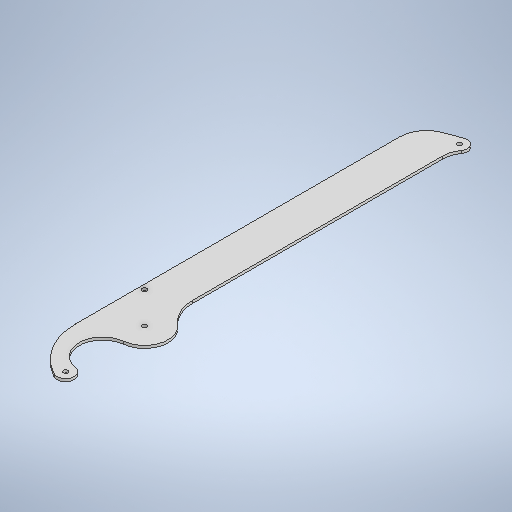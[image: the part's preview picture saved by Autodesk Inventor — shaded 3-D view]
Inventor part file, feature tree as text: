
AUTODESK INVENTOR PART (.ipt)
format: ipt  version: 2025.2 (Build 292293000, 293)  size: 292,864 bytes
history: native  units: in
note: dims shown in document units (in); Inventor stores cm internally (conversion verified against a paired STEP export)
features: extrude x2, sketch x2
ambient origin geometry x8: Origin, YZ Plane, XZ Plane, XY Plane, X Axis, Y Axis, Z Axis, Center Point
bodies: Solid1 (feature_tree)
feature tree (4):
  extrude  "Extrusion1"  Depth=1.9685in
  extrude  "Extrusion2"  Depth=0.0669in TaperAngle=0.0deg
  sketch  "Sketch1"  dims[d0=0.4291in d1=1.9685in]
  sketch  "Sketch2"  dims[d4=7.874in d5=0.0669in d6=0.0in d7=0.1181in d8=0.1181in d9=0.7874in d10=0.7874in d11=0.1181in d12=0.1181in d13=0.0669in d14=0.0in d15=0.0in d16=0.5906in d17=0.0in d18=0.5906in]
